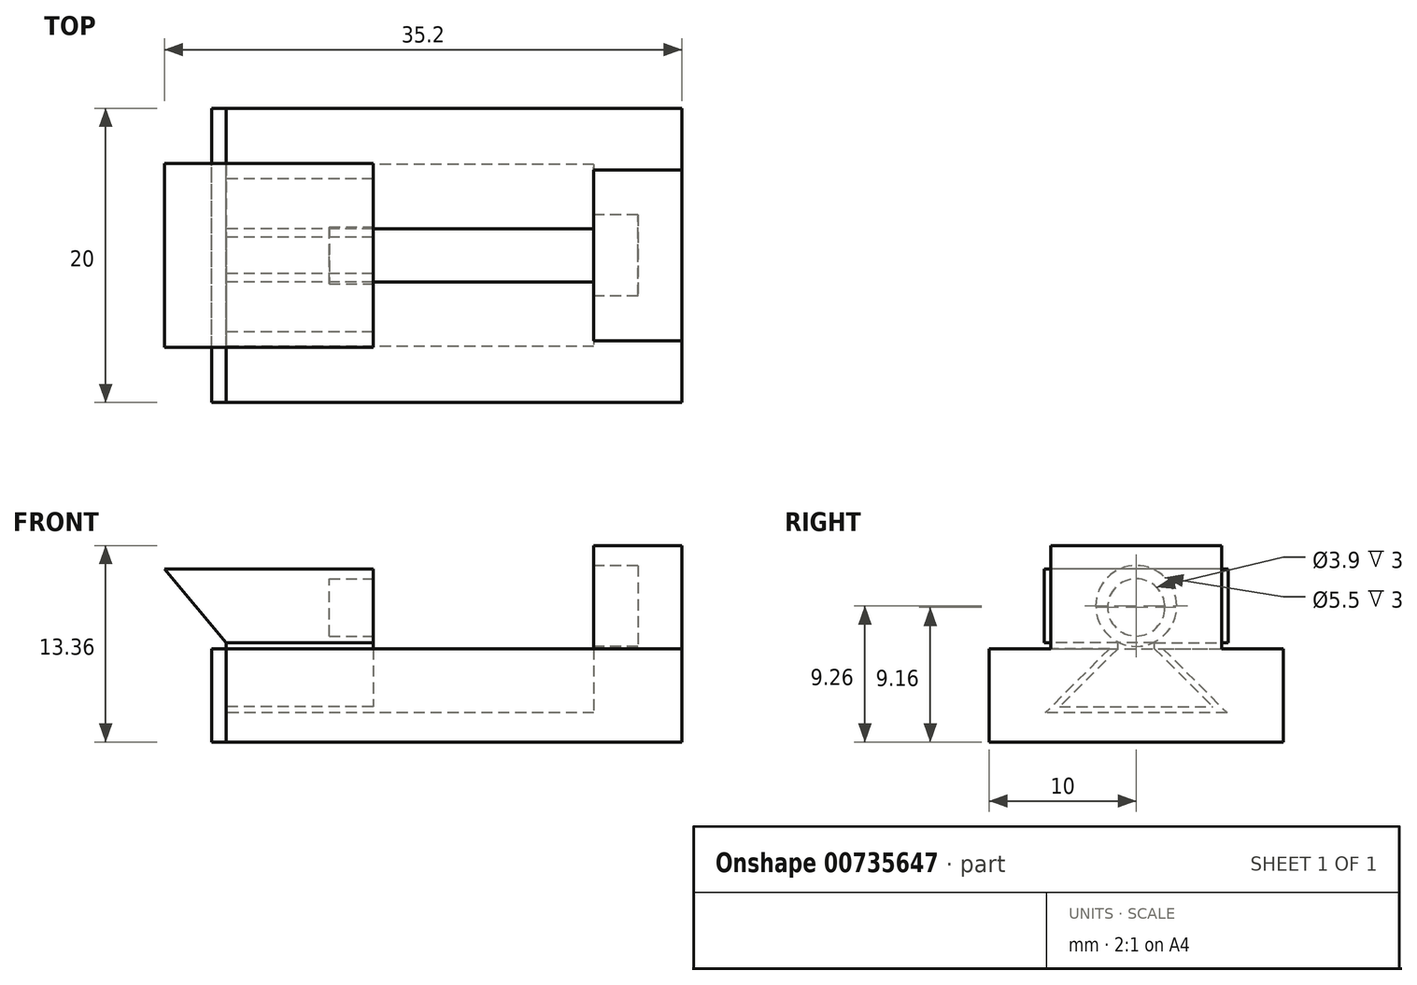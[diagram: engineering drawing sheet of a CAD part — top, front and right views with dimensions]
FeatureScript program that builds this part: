
annotation { "Feature Type Name" : "Feature", "Feature Type Description" : "" }
export const myFeature = defineFeature(function(context is Context, id is Id, definition is map)
    precondition{}
    {
        {
            assignVariable(context, id + "F0", {"name" : "Schieber_l", "anyValue" : 10});
        }
        {
            var Q0;
            Q0=qCreatedBy(makeId("Right.planeOp"),FACE);
            var sketch = newSketch(context, id + "F1", { "sketchPlane" : qUnion([Q0])});
            skLineSegment(sketch, "E0", {"start": v(10, 0) * mm, "end": v(10, -6.36) * mm});
            skLineSegment(sketch, "E1", {"start": v(10, -6.36) * mm, "end": v(0, -6.36) * mm});
            skLineSegment(sketch, "E2", {"start": v(0, 0) * mm, "end": v(1.82, 0) * mm, "construction": true});
            skLineSegment(sketch, "E3", {"start": v(1.82, 0) * mm, "end": v(10, 0) * mm});
            skLineSegment(sketch, "E4", {"start": v(6.18, -4.36) * mm, "end": v(0, -4.36) * mm});
            skLineSegment(sketch, "E5", {"start": v(0, 0) * mm, "end": v(0, -6.36) * mm, "construction": true});
            skLineSegment(sketch, "E6.MirrorCS", {"start": v(0, 0) * mm, "end": v(-1.82, 0) * mm, "construction": true});
            skLineSegment(sketch, "E7.MirrorCS", {"start": v(-1.82, 0) * mm, "end": v(-10, 0) * mm});
            skLineSegment(sketch, "E8.MirrorCS", {"start": v(-10, -6.36) * mm, "end": v(0, -6.36) * mm});
            skLineSegment(sketch, "E9.MirrorCS", {"start": v(-10, 0) * mm, "end": v(-10, -6.36) * mm});
            skLineSegment(sketch, "E10.3", {"start": v(5.21, -3.96) * mm, "end": v(0, -3.96) * mm});
            skLineSegment(sketch, "E11", {"start": v(1.25, 0) * mm, "end": v(1.25, 0.4) * mm});
            skLineSegment(sketch, "E12", {"start": v(1.25, 0.4) * mm, "end": v(6.25, 0.4) * mm});
            skLineSegment(sketch, "E13", {"start": v(6.25, 0.4) * mm, "end": v(6.25, 5.4) * mm});
            skLineSegment(sketch, "E14", {"start": v(6.25, 5.4) * mm, "end": v(0, 5.4) * mm});
            skLineSegment(sketch, "E15.MirrorCS", {"start": v(-1.25, 0) * mm, "end": v(-1.25, 0.4) * mm});
            skLineSegment(sketch, "E16.MirrorCS", {"start": v(-1.25, 0.4) * mm, "end": v(-6.25, 0.4) * mm});
            skLineSegment(sketch, "E17.MirrorCS", {"start": v(-6.25, 0.4) * mm, "end": v(-6.25, 5.4) * mm});
            skLineSegment(sketch, "E18.MirrorCS", {"start": v(-6.25, 5.4) * mm, "end": v(0, 5.4) * mm});
            skLineSegment(sketch, "E19", {"start": v(1.25, 0) * mm, "end": v(5.21, -3.96) * mm});
            skLineSegment(sketch, "E20", {"start": v(1.82, 0) * mm, "end": v(6.18, -4.36) * mm});
            skLineSegment(sketch, "E21.MirrorCS", {"start": v(-5.21, -3.96) * mm, "end": v(0, -3.96) * mm});
            skLineSegment(sketch, "E22.MirrorCS", {"start": v(-6.18, -4.36) * mm, "end": v(0, -4.36) * mm});
            skLineSegment(sketch, "E23.MirrorCS", {"start": v(-1.25, 0) * mm, "end": v(-5.21, -3.96) * mm});
            skLineSegment(sketch, "E24.MirrorCS", {"start": v(-1.82, 0) * mm, "end": v(-6.18, -4.36) * mm});
            skSolve(sketch);
        }
        {
            var Q0;
            Q0=makeQuery(id+"F1.imprint","IMPRINT",FACE,{"disambiguationData":[TD([[makeQuery(id+"F1.imprint","IMPRINT",EDGE,{"derivedFrom":sQuery(id+"F1.wireOp",EDGE,"E0")}),-1.0]])]});
            extrude(context, id + "F2", {"entities" : qUnion([Q0]), "depth" : 25 * mm, "offsetDistance" : 25 * mm});
        }
        {
            var Q0;
            Q0=makeQuery(id+"F1.imprint","IMPRINT",FACE,{"disambiguationData":[TD([[makeQuery(id+"F1.imprint","IMPRINT",EDGE,{"derivedFrom":sQuery(id+"F1.wireOp",EDGE,"E10.0")}),-1.0]])]});
            var Q1;
            Q1=makeQuery(id+"F1.imprint","IMPRINT",FACE,{"disambiguationData":[TD([[makeQuery(id+"F1.imprint","IMPRINT",EDGE,{"derivedFrom":sQuery(id+"F1.wireOp",EDGE,"E10.3")}),-1.0]])]});
            extrude(context, id + "F3", {"entities" : qUnion([Q0, Q1]), "depth" : (getVariable(context, 'Schieber_l')) * mm, "offsetDistance" : 25 * mm});
        }
        {
            var Q0;
            Q0=makeQuery(id+"F3.opExtrude","SWEPT_FACE",FACE,{"disambiguationData":[OSD([sQuery(id+"F1.wireOp",EDGE,"E17.MirrorCS")])]});
            var sketch = newSketch(context, id + "F4", { "sketchPlane" : qUnion([Q0])});
            skLineSegment(sketch, "E25", {"start": v(0, 0.4) * mm, "end": v(-4.2, 5.4) * mm});
            skLineSegment(sketch, "E26", {"start": v(-4.2, 5.4) * mm, "end": v(0, 5.4) * mm});
            skSolve(sketch);
        }
        {
            var Q0;
            Q0=makeQuery(id+"F4.imprint","IMPRINT",FACE,{"disambiguationData":[TD([[makeQuery(id+"F4.imprint","IMPRINT",EDGE,{"derivedFrom":sQuery(id+"F4.wireOp",EDGE,"E25")}),-1.0]])]});
            var Q1;
            Q1=makeQuery(id+"F3.opExtrude","SWEPT_FACE",FACE,{"disambiguationData":[OSD([sQuery(id+"F1.wireOp",EDGE,"E13")])]});
            extrude(context, id + "F5", {"entities" : qUnion([Q0]), "operationType" : NewBodyOperationType.ADD, "endBound" : BoundingType.UP_TO_SURFACE, "oppositeDirection" : true, "depth" : 25 * mm, "endBoundEntityFace" : qUnion([Q1]), "offsetDistance" : 25 * mm});
        }
        {
            var Q0;
            Q0=makeQuery(id+"F2.opExtrude","CAP_FACE",FACE,{"disambiguationData":[OSD([sQuery(id+"F1.wireOp",EDGE,"E0"),sQuery(id+"F1.wireOp",EDGE,"E1"),sQuery(id+"F1.wireOp",EDGE,"E3"),sQuery(id+"F1.wireOp",EDGE,"uL4fXtI6-5IPU-LAWi-0ZZa-cN97hL0aCCqk"),sQuery(id+"F1.wireOp",EDGE,"AKZl68VK-38FB-Ht4s-vepi-rxk2rTPZP17L"),sQuery(id+"F1.wireOp",EDGE,"i5Y14g0h-S7OM-WHCa-fd2H-VGr6gsvA6Dlt"),sQuery(id+"F1.wireOp",EDGE,"E4"),sQuery(id+"F1.wireOp",EDGE,"c9294c27-b3fc-48be-944e-fddcc5ddd1fd0.MirrorCS"),sQuery(id+"F1.wireOp",EDGE,"c9294c27-b3fc-48be-944e-fddcc5ddd1fd2.MirrorCS"),sQuery(id+"F1.wireOp",EDGE,"c9294c27-b3fc-48be-944e-fddcc5ddd1fd3.MirrorCS"),sQuery(id+"F1.wireOp",EDGE,"E7.MirrorCS"),sQuery(id+"F1.wireOp",EDGE,"E8.MirrorCS"),sQuery(id+"F1.wireOp",EDGE,"E9.MirrorCS"),sQuery(id+"F1.wireOp",EDGE,"c9294c27-b3fc-48be-944e-fddcc5ddd1fd7.MirrorCS")])],"isStart":false});
            var sketch = newSketch(context, id + "F6", { "sketchPlane" : qUnion([Q0])});
            skLineSegment(sketch, "E27", {"start": v(-1.82, 0) * mm, "end": v(10, 0) * mm});
            skSolve(sketch);
        }
        {
            var Q0;
            Q0=makeQuery(id+"F6.imprint","IMPRINT",FACE,{"disambiguationData":[TD([[makeQuery(id+"F6.imprint","IMPRINT",EDGE,{"derivedFrom":makeQuery(id+"F2.opExtrude","CAP_EDGE",EDGE,{"disambiguationData":[OSD([sQuery(id+"F1.wireOp",EDGE,"E0")])],"isStart":false})}),-1.0]])]});
            var Q1;
            Q1=makeQuery(id+"F6.imprint","IMPRINT",FACE,{"disambiguationData":[TD([[makeQuery(id+"F6.imprint","IMPRINT",EDGE,{"derivedFrom":sQuery(id+"F6.wireOp",EDGE,"E27")}),-1.0]])]});
            extrude(context, id + "F7", {"entities" : qUnion([Q0, Q1]), "operationType" : NewBodyOperationType.ADD, "depth" : 6 * mm, "offsetDistance" : 25 * mm});
        }
        {
            var Q0;
            {var subQ0=sQuery(id+"F1.wireOp",EDGE,"E7.MirrorCS");var subQ1=sQuery(id+"F1.wireOp",EDGE,"E3");Q0=makeQuery(id+"F7.boolean.opBoolean","MERGE",FACE,{"derivedFrom":[makeQuery(id+"F2.opExtrude","SWEPT_FACE",FACE,{"disambiguationData":[OSD([subQ1])]}),makeQuery(id+"F2.opExtrude","SWEPT_FACE",FACE,{"disambiguationData":[OSD([subQ0])]}),makeQuery(id+"F7.opExtrude","SWEPT_FACE",FACE,{"disambiguationData":[OSD([subQ1,subQ0,sQuery(id+"F6.wireOp",EDGE,"E27")])]})]});}
            var sketch = newSketch(context, id + "F8", { "sketchPlane" : qUnion([Q0])});
            skLineSegment(sketch, "E28", {"start": v(25, -1.82) * mm, "end": v(25, -10) * mm});
            skLineSegment(sketch, "E29", {"start": v(25, 1.82) * mm, "end": v(25, 10) * mm});
            skLineSegment(sketch, "E30", {"start": v(25, 5.82) * mm, "end": v(31, 5.82) * mm});
            skLineSegment(sketch, "E31", {"start": v(25, -5.82) * mm, "end": v(31, -5.82) * mm});
            skSolve(sketch);
        }
        {
            var Q0;
            Q0 = qSketchRegion(id + "F8", true);
            var Q1;
            {var subQ0=sQuery(id+"F8.wireOp",EDGE,"E30");Q1=makeQuery(id+"F8.imprint","IMPRINT",FACE,{"disambiguationData":[TD([[makeQuery(id+"F8.imprint","IMPRINT",EDGE,{"derivedFrom":subQ0}),-1.0]])]});}
            extrude(context, id + "F9", {"entities" : qUnion([Q0, Q1]), "operationType" : NewBodyOperationType.ADD, "depth" : 7 * mm, "offsetDistance" : 25 * mm});
        }
        {
            var Q0;
            {var subQ0=sQuery(id+"F6.wireOp",EDGE,"E27");var subQ1=sQuery(id+"F1.wireOp",EDGE,"E7.MirrorCS");var subQ2=sQuery(id+"F1.wireOp",EDGE,"E3");Q0=makeQuery(id+"F9.boolean.opBoolean","MERGE",FACE,{"derivedFrom":[makeQuery(id+"F7.opExtrude","CAP_FACE",FACE,{"disambiguationData":[OSD([sQuery(id+"F1.wireOp",EDGE,"E0"),sQuery(id+"F1.wireOp",EDGE,"E1"),subQ2,subQ1,sQuery(id+"F1.wireOp",EDGE,"E8.MirrorCS"),sQuery(id+"F1.wireOp",EDGE,"E9.MirrorCS"),subQ0])],"isStart":true}),makeQuery(id+"F9.opExtrude","SWEPT_FACE",FACE,{"disambiguationData":[OSD([subQ2,subQ1,subQ0,sQuery(id+"F8.wireOp",EDGE,"E28"),sQuery(id+"F8.wireOp",EDGE,"E29")])]})]});}
            var sketch = newSketch(context, id + "F10", { "sketchPlane" : qUnion([Q0])});
            skLineSegment(sketch, "E32.0.0", {"start": v(-6.25, 5.4) * mm, "end": v(6.25, 5.4) * mm});
            skLineSegment(sketch, "E32.0.1", {"start": v(6.25, 5.4) * mm, "end": v(6.25, 0.4) * mm});
            skLineSegment(sketch, "E32.0.2", {"start": v(6.25, 0.4) * mm, "end": v(1.25, 0.4) * mm});
            skLineSegment(sketch, "E32.0.3", {"start": v(1.25, 0.4) * mm, "end": v(1.25, -2.3) * mm});
            skLineSegment(sketch, "E32.0.4", {"start": v(1.25, -2.3) * mm, "end": v(5.7, -2.3) * mm});
            skLineSegment(sketch, "E32.0.5", {"start": v(5.7, -2.3) * mm, "end": v(5.7, -3.96) * mm});
            skLineSegment(sketch, "E32.0.6", {"start": v(5.7, -3.96) * mm, "end": v(-5.21, -3.96) * mm});
            skLineSegment(sketch, "E32.0.7", {"start": v(-5.21, -3.96) * mm, "end": v(-5.21, -0.56) * mm});
            skLineSegment(sketch, "E32.0.8", {"start": v(-5.21, -0.56) * mm, "end": v(-1.25, -0.56) * mm});
            skLineSegment(sketch, "E32.0.9", {"start": v(-1.25, -0.56) * mm, "end": v(-1.25, 0.4) * mm});
            skLineSegment(sketch, "E32.0.10", {"start": v(-1.25, 0.4) * mm, "end": v(-6.25, 0.4) * mm});
            skLineSegment(sketch, "E32.0.11", {"start": v(-6.25, 0.4) * mm, "end": v(-6.25, 5.4) * mm});
            skLineSegment(sketch, "E33", {"start": v(-6.25, 5.4) * mm, "end": v(6.25, 0.4) * mm, "construction": true});
            skCircle(sketch, "E34", {"center": v(0, 2.9) * mm, "radius": 2.75 * mm});
            skSolve(sketch);
        }
        {
            var Q0;
            Q0=makeQuery(id+"F10.imprint","IMPRINT",FACE,{"disambiguationData":[TD([[makeQuery(id+"F10.imprint","IMPRINT",EDGE,{"derivedFrom":sQuery(id+"F10.wireOp",EDGE,"cOLPNfTv-siIc-Wv7O-LUPw-DwOUoxpCxWV8")}),1.0]])]});
            var Q1;
            Q1=makeQuery(id+"F10.imprint","IMPRINT",FACE,{"disambiguationData":[TD([[makeQuery(id+"F10.imprint","IMPRINT",EDGE,{"derivedFrom":sQuery(id+"F10.wireOp",EDGE,"E34")}),1.0]])]});
            extrude(context, id + "F11", {"entities" : qUnion([Q0, Q1]), "operationType" : NewBodyOperationType.REMOVE, "oppositeDirection" : true, "depth" : 3 * mm, "offsetDistance" : 25 * mm});
        }
        {
            var Q0;
            Q0=makeQuery(id+"F3.opExtrude","CAP_FACE",FACE,{"disambiguationData":[OSD([sQuery(id+"F1.wireOp",EDGE,"E10.0"),sQuery(id+"F1.wireOp",EDGE,"E10.1"),sQuery(id+"F1.wireOp",EDGE,"E10.2"),sQuery(id+"F1.wireOp",EDGE,"E10.3"),sQuery(id+"F1.wireOp",EDGE,"E11"),sQuery(id+"F1.wireOp",EDGE,"E12"),sQuery(id+"F1.wireOp",EDGE,"E13"),sQuery(id+"F1.wireOp",EDGE,"E14"),sQuery(id+"F1.wireOp",EDGE,"bdd6576c-31a5-4fe6-8e7b-b9710d8a2b690.MirrorCS"),sQuery(id+"F1.wireOp",EDGE,"655eb150-fbf2-40c7-927d-945109eecf380.MirrorCS"),sQuery(id+"F1.wireOp",EDGE,"0841a61a-c7ab-45ac-85f3-7b15b5edff330.MirrorCS"),sQuery(id+"F1.wireOp",EDGE,"fd4d8c7c-1ef8-41f7-855c-a76f163565710.MirrorCS"),sQuery(id+"F1.wireOp",EDGE,"E15.MirrorCS"),sQuery(id+"F1.wireOp",EDGE,"E16.MirrorCS"),sQuery(id+"F1.wireOp",EDGE,"E17.MirrorCS"),sQuery(id+"F1.wireOp",EDGE,"E18.MirrorCS")])],"isStart":false});
            var sketch = newSketch(context, id + "F12", { "sketchPlane" : qUnion([Q0])});
            skCircle(sketch, "E35.0", {"center": v(0, 2.8) * mm, "radius": 1 * mm});
            skCircle(sketch, "E36", {"center": v(0, 2.8) * mm, "radius": 1.95 * mm});
            skSolve(sketch);
        }
        {
            var Q0;
            Q0=makeQuery(id+"F12.imprint","IMPRINT",FACE,{"disambiguationData":[TD([[makeQuery(id+"F12.imprint","IMPRINT",EDGE,{"derivedFrom":sQuery(id+"F12.wireOp",EDGE,"E35.0")}),-1.0]])]});
            var Q1;
            Q1=makeQuery(id+"F12.imprint","IMPRINT",FACE,{"disambiguationData":[TD([[makeQuery(id+"F12.imprint","IMPRINT",EDGE,{"derivedFrom":sQuery(id+"F12.wireOp",EDGE,"E35.0")}),1.0]])]});
            extrude(context, id + "F13", {"entities" : qUnion([Q0, Q1]), "operationType" : NewBodyOperationType.REMOVE, "oppositeDirection" : true, "depth" : 3 * mm, "offsetDistance" : 25 * mm});
        }
        {
            var Q0;
            Q0=makeQuery(id+"F1.imprint","IMPRINT",FACE,{"disambiguationData":[TD([[makeQuery(id+"F1.imprint","IMPRINT",EDGE,{"derivedFrom":sQuery(id+"F1.wireOp",EDGE,"E0")}),-1.0]])]});
            var sketch = newSketch(context, id + "F14", { "sketchPlane" : qUnion([Q0])});
            skLineSegment(sketch, "E37.0.0", {"start": v(4.18, -0.36) * mm, "end": v(4.18, 0) * mm});
            skLineSegment(sketch, "E37.0.1", {"start": v(4.18, 0) * mm, "end": v(-10, 0) * mm});
            skLineSegment(sketch, "E37.0.2", {"start": v(-10, 0) * mm, "end": v(-10, -6.36) * mm});
            skLineSegment(sketch, "E37.0.3", {"start": v(-10, -6.36) * mm, "end": v(0, -6.36) * mm});
            skLineSegment(sketch, "E37.0.4", {"start": v(0, -6.36) * mm, "end": v(10, -6.36) * mm});
            skLineSegment(sketch, "E37.0.5", {"start": v(10, -6.36) * mm, "end": v(10, 0) * mm});
            skLineSegment(sketch, "E37.0.6", {"start": v(10, 0) * mm, "end": v(10, 0) * mm});
            skLineSegment(sketch, "E37.0.7", {"start": v(10, 0) * mm, "end": v(10, -2) * mm});
            skLineSegment(sketch, "E37.0.8", {"start": v(6, -2) * mm, "end": v(10, -2) * mm});
            skLineSegment(sketch, "E37.0.9", {"start": v(6, -2) * mm, "end": v(6, -4.36) * mm});
            skLineSegment(sketch, "E37.0.10", {"start": v(6.18, -4.36) * mm, "end": v(6, -4.36) * mm});
            skLineSegment(sketch, "E37.0.11", {"start": v(6.18, -4.36) * mm, "end": v(0.18, -4.36) * mm});
            skLineSegment(sketch, "E37.0.12", {"start": v(0.18, -4.36) * mm, "end": v(0.18, -0.36) * mm});
            skLineSegment(sketch, "E37.0.13", {"start": v(0.18, -0.36) * mm, "end": v(4.18, -0.36) * mm});
            skLineSegment(sketch, "E38", {"start": v(10, 0) * mm, "end": v(4.18, 0) * mm});
            skSolve(sketch);
        }
        {
            var Q0;
            Q0 = qSketchRegion(id + "F14", true);
            extrude(context, id + "F15", {"entities" : qUnion([Q0]), "oppositeDirection" : true, "depth" : 1 * mm, "offsetDistance" : 25 * mm});
        }
    });
